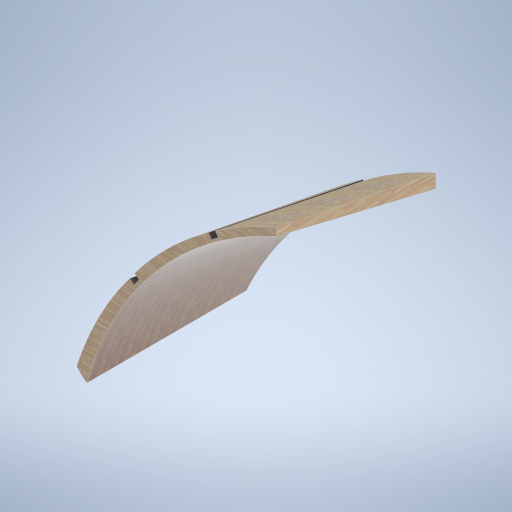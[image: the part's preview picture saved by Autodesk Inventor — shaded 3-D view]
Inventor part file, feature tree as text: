
AUTODESK INVENTOR PART (.ipt)
format: ipt  version: 2024.2 (Build 282272000, 272)  size: 491,520 bytes
history: native  units: mm
features: sketch x12, loft x5, plane x2
ambient origin geometry x8: Origin, YZ Plane, XZ Plane, XY Plane, X Axis, Y Axis, Z Axis, Center Point
bodies: Solid1 (feature_tree)
feature tree (19):
  sketch  "Sketch2"  dims[d3=8500.0mm d4=8500.0mm d5=8500.0mm d6=0.0mm d7=3749.0mm]
  plane  "Work Plane2"
  sketch  "Sketch3"  dims[d8=8500.0mm d9=0.0mm d10=90.0deg]
  loft  "Loft1"
  loft  "Loft2"
  loft  "Loft3"
  loft  "Loft4"
  loft  "Loft5"
  plane  "Work Plane1"
  sketch  "Sketch6"  dims[d11=0.0mm d12=90.0deg d13=8000.0mm]
  sketch  "Sketch7"  dims[d14=0.0mm d15=90.0deg d16=0.0mm d17=90.0deg]
  sketch  "Sketch8"  dims[d18=8500.0mm d19=0.0mm d20=90.0deg]
  sketch  "Sketch9"  dims[d21=0.0mm d22=90.0deg]
  sketch  "Sketch10"  dims[d23=8000.0mm]
  sketch  "Sketch11"  dims[d24=0.0mm d25=90.0deg]
  sketch  "Sketch13"  dims[d26=0.0mm d27=90.0deg]
  sketch  "Sketch14"  dims[d28=8000.0mm]
  sketch  "Sketch15"  dims[d29=8500.0mm]
  sketch  "Sketch18"  dims[d30=0.0mm d31=90.0deg d32=0.0mm d33=90.0deg]
